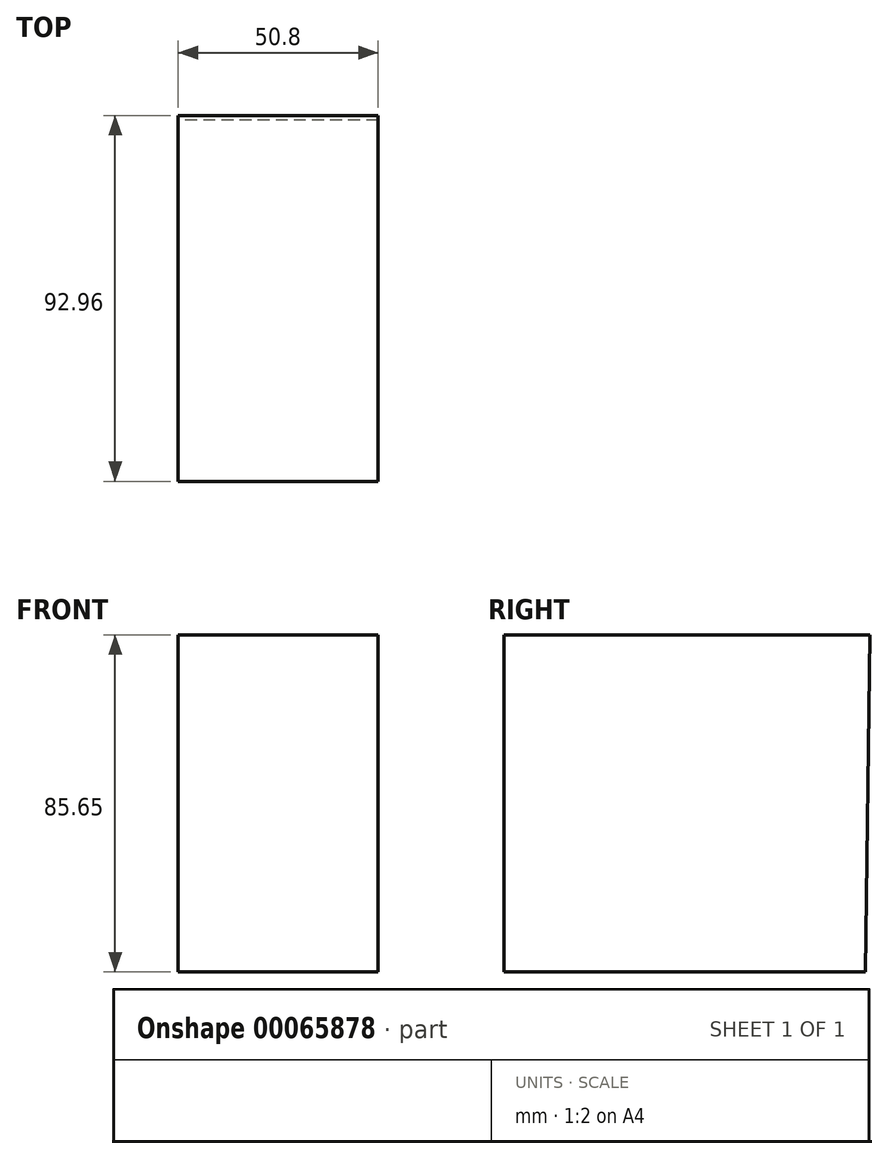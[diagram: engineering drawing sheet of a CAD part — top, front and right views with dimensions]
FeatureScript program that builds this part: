
annotation { "Feature Type Name" : "Feature", "Feature Type Description" : "" }
export const myFeature = defineFeature(function(context is Context, id is Id, definition is map)
    precondition{}
    {
        {
            var Q0;
            Q0=qCreatedBy(makeId("Right.planeOp"),FACE);
            var sketch = newSketch(context, id + "F0", { "sketchPlane" : qUnion([Q0])});
            skPoint(sketch, "E0", {"position": v(48.46, 45.57) * mm});
            skPoint(sketch, "E1", {"position": v(-44.5, 45.57) * mm});
            skLineSegment(sketch, "E2", {"start": v(-44.5, 45.57) * mm, "end": v(48.46, 45.57) * mm});
            skLineSegment(sketch, "E3", {"start": v(-44.5, 45.57) * mm, "end": v(-44.5, -40.08) * mm});
            skLineSegment(sketch, "E4", {"start": v(-44.5, -40.08) * mm, "end": v(47.24, -40.08) * mm});
            skLineSegment(sketch, "E5", {"start": v(47.24, -40.08) * mm, "end": v(48.46, 45.57) * mm});
            skLineSegment(sketch, "E6", {"start": v(48.46, 45.57) * mm, "end": v(-44.5, 45.57) * mm});
            skLineSegment(sketch, "E7", {"start": v(48.46, 45.57) * mm, "end": v(47.24, -40.08) * mm});
            skSolve(sketch);
        }
        {
            var Q0;
            Q0 = qSketchRegion(id + "F0", true);
            extrude(context, id + "F1", {"entities" : qUnion([Q0]), "depth" : 25.4 * mm});
        }
        {
            var Q0;
            Q0=makeQuery(id+"F1.opExtrude","CAP_FACE",FACE,{"disambiguationData":[OSD([sQuery(id+"F0.wireOp",EDGE,"E3"),sQuery(id+"F0.wireOp",EDGE,"E4"),sQuery(id+"F0.wireOp",EDGE,"E6"),sQuery(id+"F0.wireOp",EDGE,"E7")])],"isStart":false});
            extrude(context, id + "F2", {"entities" : qUnion([Q0]), "operationType" : NewBodyOperationType.ADD, "depth" : 25.4 * mm});
        }
    });
